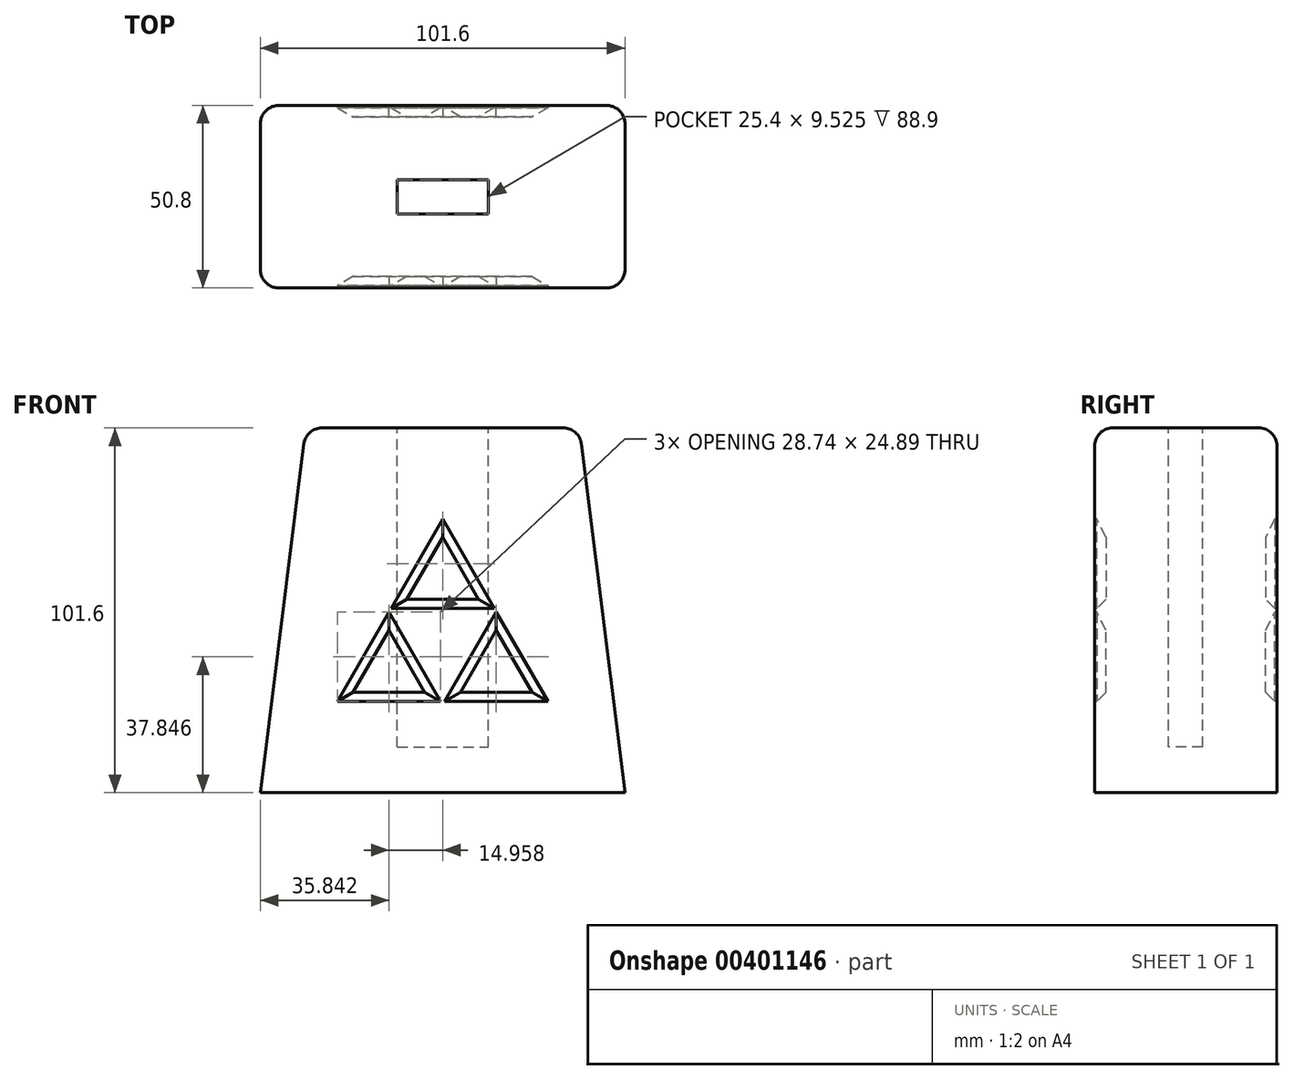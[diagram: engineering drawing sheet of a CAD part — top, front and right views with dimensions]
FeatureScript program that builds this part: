
annotation { "Feature Type Name" : "Feature", "Feature Type Description" : "" }
export const myFeature = defineFeature(function(context is Context, id is Id, definition is map)
    precondition{}
    {
        {
            var Q0;
            Q0=qCreatedBy(makeId("Top.planeOp"),FACE);
            var sketch = newSketch(context, id + "F0", { "sketchPlane" : qUnion([Q0])});
            skLineSegment(sketch, "E0.bottom", {"start": v(-50.8, 25.4) * mm, "end": v(50.8, 25.4) * mm});
            skLineSegment(sketch, "E0.top", {"start": v(-50.8, -25.4) * mm, "end": v(50.8, -25.4) * mm});
            skLineSegment(sketch, "E0.left", {"start": v(-50.8, 25.4) * mm, "end": v(-50.8, -25.4) * mm});
            skLineSegment(sketch, "E0.right", {"start": v(50.8, 25.4) * mm, "end": v(50.8, -25.4) * mm});
            skPoint(sketch, "E0.middle", {"position": v(0, 0) * mm});
            skSolve(sketch);
        }
        {
            var Q0;
            Q0 = qSketchRegion(id + "F0", true);
            extrude(context, id + "F1", {"entities" : qUnion([Q0]), "depth" : 101.6 * mm});
        }
        {
            var Q0;
            Q0=makeQuery(id+"F1.opExtrude","CAP_EDGE",EDGE,{"disambiguationData":[OSD([sQuery(id+"F0.wireOp",EDGE,"E0.right")])],"isStart":false});
            var Q1;
            Q1=makeQuery(id+"F1.opExtrude","CAP_EDGE",EDGE,{"disambiguationData":[OSD([sQuery(id+"F0.wireOp",EDGE,"E0.left")])],"isStart":false});
            chamfer(context, id + "F2", {"entities" : qUnion([Q0, Q1]), "chamferType" : ChamferType.TWO_OFFSETS, "width1" : 101.6 * mm, "oppositeDirection" : false, "width2" : 12.7 * mm, "tangentPropagation" : true});
        }
        {
            var Q0;
            Q0=makeQuery(id+"F1.opExtrude","SWEPT_FACE",FACE,{"disambiguationData":[OSD([sQuery(id+"F0.wireOp",EDGE,"E0.top")])]});
            var sketch = newSketch(context, id + "F3", { "sketchPlane" : qUnion([Q0])});
            skLineSegment(sketch, "E1", {"start": v(0, 76.2) * mm, "end": v(-29.33, 25.4) * mm});
            skPoint(sketch, "E1.startSnap0", {"position": v(0, 101.6) * mm});
            skLineSegment(sketch, "E2", {"start": v(-29.33, 25.4) * mm, "end": v(0, 25.4) * mm});
            skLineSegment(sketch, "E3", {"start": v(0, 25.4) * mm, "end": v(0, 76.2) * mm});
            skLineSegment(sketch, "E4.MirrorCS", {"start": v(0, 76.2) * mm, "end": v(29.33, 25.4) * mm});
            skLineSegment(sketch, "E5.MirrorCS", {"start": v(29.33, 25.4) * mm, "end": v(0, 25.4) * mm});
            skSolve(sketch);
        }
        {
            var Q0;
            Q0=makeQuery(id+"F3.imprint","IMPRINT",FACE,{"disambiguationData":[TD([[makeQuery(id+"F3.imprint","IMPRINT",EDGE,{"derivedFrom":sQuery(id+"F3.wireOp",EDGE,"E1")}),1.0]])]});
            var Q1;
            Q1=makeQuery(id+"F3.imprint","IMPRINT",FACE,{"disambiguationData":[TD([[makeQuery(id+"F3.imprint","IMPRINT",EDGE,{"derivedFrom":sQuery(id+"F3.wireOp",EDGE,"E3")}),-1.0]])]});
            extrude(context, id + "F4", {"entities" : qUnion([Q0, Q1]), "operationType" : NewBodyOperationType.REMOVE, "oppositeDirection" : true, "depth" : 3.17 * mm});
        }
        {
            var Q0;
            Q0 = qSketchRegion(id + "F3", true);
            extrude(context, id + "F5", {"entities" : qUnion([Q0]), "operationType" : NewBodyOperationType.REMOVE, "oppositeDirection" : true, "depth" : 103.89 * mm, "hasSecondDirection" : true, "secondDirectionOppositeDirection" : true, "secondDirectionDepth" : 47.62 * mm});
        }
        {
            var Q0;
            Q0=makeQuery(id+"F5.boolean.opBoolean","COPY",FACE,{"derivedFrom":makeQuery(id+"F5.opExtrude","CAP_FACE",FACE,{"disambiguationData":[OSD([sQuery(id+"F3.wireOp",EDGE,"E1"),sQuery(id+"F3.wireOp",EDGE,"E2"),sQuery(id+"F3.wireOp",EDGE,"E4.MirrorCS"),sQuery(id+"F3.wireOp",EDGE,"E5.MirrorCS")])],"isStart":true})});
            var sketch = newSketch(context, id + "F6", { "sketchPlane" : qUnion([Q0])});
            skLineSegment(sketch, "E6", {"start": v(-14.66, 50.8) * mm, "end": v(-15.54, 51.3) * mm});
            skLineSegment(sketch, "E7", {"start": v(14.66, 50.8) * mm, "end": v(15.54, 51.3) * mm});
            skLineSegment(sketch, "E8", {"start": v(0, 25.4) * mm, "end": v(0, 24.38) * mm});
            skPoint(sketch, "E8.endSnap0", {"position": v(0, 25.4) * mm});
            skLineSegment(sketch, "E9", {"start": v(-15.54, 51.3) * mm, "end": v(15.54, 51.3) * mm});
            skLineSegment(sketch, "E10", {"start": v(0, 24.38) * mm, "end": v(-15.54, 51.3) * mm});
            skLineSegment(sketch, "E11", {"start": v(15.54, 51.3) * mm, "end": v(0, 24.38) * mm});
            skSolve(sketch);
        }
        {
            var Q0;
            Q0 = qSketchRegion(id + "F6", true);
            var Q1;
            Q1=makeQuery(id+"F1.opExtrude","SWEPT_FACE",FACE,{"disambiguationData":[OSD([sQuery(id+"F0.wireOp",EDGE,"E0.bottom")])]});
            var Q2;
            Q2=makeQuery(id+"F1.opExtrude","SWEPT_FACE",FACE,{"disambiguationData":[OSD([sQuery(id+"F0.wireOp",EDGE,"E0.top")])]});
            extrude(context, id + "F7", {"entities" : qUnion([Q0]), "operationType" : NewBodyOperationType.ADD, "endBound" : BoundingType.UP_TO_SURFACE, "endBoundEntityFace" : qUnion([Q1]), "depth" : 25.4 * mm, "hasSecondDirection" : true, "secondDirectionBound" : SecondDirectionBoundingType.UP_TO_SURFACE, "secondDirectionOppositeDirection" : true, "secondDirectionBoundEntityFace" : qUnion([Q2]), "secondDirectionDepth" : 25.4 * mm});
        }
        {
            var Q0;
            Q0=makeQuery(id+"F1.opExtrude","CAP_FACE",FACE,{"disambiguationData":[OSD([sQuery(id+"F0.wireOp",EDGE,"E0.bottom"),sQuery(id+"F0.wireOp",EDGE,"E0.top"),sQuery(id+"F0.wireOp",EDGE,"E0.left"),sQuery(id+"F0.wireOp",EDGE,"E0.right")])],"isStart":false});
            var sketch = newSketch(context, id + "F8", { "sketchPlane" : qUnion([Q0])});
            skLineSegment(sketch, "E12.bottom", {"start": v(-12.7, 4.76) * mm, "end": v(12.7, 4.76) * mm});
            skLineSegment(sketch, "E12.top", {"start": v(-12.7, -4.76) * mm, "end": v(12.7, -4.76) * mm});
            skLineSegment(sketch, "E12.left", {"start": v(-12.7, 4.76) * mm, "end": v(-12.7, -4.76) * mm});
            skLineSegment(sketch, "E12.right", {"start": v(12.7, 4.76) * mm, "end": v(12.7, -4.76) * mm});
            skPoint(sketch, "E12.middle", {"position": v(0, 0) * mm});
            skSolve(sketch);
        }
        {
            var Q0;
            Q0 = qSketchRegion(id + "F8", true);
            extrude(context, id + "F9", {"entities" : qUnion([Q0]), "operationType" : NewBodyOperationType.REMOVE, "oppositeDirection" : true, "depth" : 88.9 * mm});
        }
        {
            var Q0;
            {var subQ0=sQuery(id+"F0.wireOp",EDGE,"E0.left");Q0=makeQuery(id+"F2.opChamfer","BLEND_EDGE",EDGE,{"blendedFrom":[makeQuery(id+"F1.opExtrude","CAP_EDGE",EDGE,{"disambiguationData":[OSD([subQ0])],"isStart":false}),makeQuery(id+"F1.opExtrude","CAP_FACE",FACE,{"disambiguationData":[OSD([sQuery(id+"F0.wireOp",EDGE,"E0.bottom"),sQuery(id+"F0.wireOp",EDGE,"E0.top"),subQ0,sQuery(id+"F0.wireOp",EDGE,"E0.right")])],"isStart":false})],"blendedInto":[makeQuery(id+"F1.opExtrude","CAP_FACE",FACE,{"disambiguationData":[OSD([sQuery(id+"F0.wireOp",EDGE,"E0.bottom"),sQuery(id+"F0.wireOp",EDGE,"E0.top"),subQ0,sQuery(id+"F0.wireOp",EDGE,"E0.right")])],"isStart":false})]});}
            var Q1;
            Q1=makeQuery(id+"F1.opExtrude","CAP_EDGE",EDGE,{"disambiguationData":[OSD([sQuery(id+"F0.wireOp",EDGE,"E0.bottom")])],"isStart":false});
            var Q2;
            {var subQ0=sQuery(id+"F0.wireOp",EDGE,"E0.right");Q2=makeQuery(id+"F2.opChamfer","BLEND_EDGE",EDGE,{"blendedFrom":[makeQuery(id+"F1.opExtrude","CAP_EDGE",EDGE,{"disambiguationData":[OSD([subQ0])],"isStart":false}),makeQuery(id+"F1.opExtrude","CAP_FACE",FACE,{"disambiguationData":[OSD([sQuery(id+"F0.wireOp",EDGE,"E0.bottom"),sQuery(id+"F0.wireOp",EDGE,"E0.top"),sQuery(id+"F0.wireOp",EDGE,"E0.left"),subQ0])],"isStart":false})],"blendedInto":[makeQuery(id+"F1.opExtrude","CAP_FACE",FACE,{"disambiguationData":[OSD([sQuery(id+"F0.wireOp",EDGE,"E0.bottom"),sQuery(id+"F0.wireOp",EDGE,"E0.top"),sQuery(id+"F0.wireOp",EDGE,"E0.left"),subQ0])],"isStart":false})]});}
            var Q3;
            Q3=makeQuery(id+"F1.opExtrude","CAP_EDGE",EDGE,{"disambiguationData":[OSD([sQuery(id+"F0.wireOp",EDGE,"E0.top")])],"isStart":false});
            var Q4;
            Q4=makeQuery(id+"F2.opChamfer","BLEND_EDGE",EDGE,{"blendedFrom":[makeQuery(id+"F1.opExtrude","CAP_EDGE",EDGE,{"disambiguationData":[OSD([sQuery(id+"F0.wireOp",EDGE,"E0.left")])],"isStart":false}),makeQuery(id+"F1.opExtrude","SWEPT_FACE",FACE,{"disambiguationData":[OSD([sQuery(id+"F0.wireOp",EDGE,"E0.bottom")])]})],"blendedInto":[makeQuery(id+"F1.opExtrude","SWEPT_FACE",FACE,{"disambiguationData":[OSD([sQuery(id+"F0.wireOp",EDGE,"E0.bottom")])]})]});
            var Q5;
            Q5=makeQuery(id+"F2.opChamfer","BLEND_EDGE",EDGE,{"blendedFrom":[makeQuery(id+"F1.opExtrude","CAP_EDGE",EDGE,{"disambiguationData":[OSD([sQuery(id+"F0.wireOp",EDGE,"E0.left")])],"isStart":false}),makeQuery(id+"F1.opExtrude","SWEPT_FACE",FACE,{"disambiguationData":[OSD([sQuery(id+"F0.wireOp",EDGE,"E0.top")])]})],"blendedInto":[makeQuery(id+"F1.opExtrude","SWEPT_FACE",FACE,{"disambiguationData":[OSD([sQuery(id+"F0.wireOp",EDGE,"E0.top")])]})]});
            var Q6;
            Q6=makeQuery(id+"F2.opChamfer","BLEND_EDGE",EDGE,{"blendedFrom":[makeQuery(id+"F1.opExtrude","CAP_EDGE",EDGE,{"disambiguationData":[OSD([sQuery(id+"F0.wireOp",EDGE,"E0.right")])],"isStart":false}),makeQuery(id+"F1.opExtrude","SWEPT_FACE",FACE,{"disambiguationData":[OSD([sQuery(id+"F0.wireOp",EDGE,"E0.bottom")])]})],"blendedInto":[makeQuery(id+"F1.opExtrude","SWEPT_FACE",FACE,{"disambiguationData":[OSD([sQuery(id+"F0.wireOp",EDGE,"E0.bottom")])]})]});
            var Q7;
            Q7=makeQuery(id+"F2.opChamfer","BLEND_EDGE",EDGE,{"blendedFrom":[makeQuery(id+"F1.opExtrude","CAP_EDGE",EDGE,{"disambiguationData":[OSD([sQuery(id+"F0.wireOp",EDGE,"E0.right")])],"isStart":false}),makeQuery(id+"F1.opExtrude","SWEPT_FACE",FACE,{"disambiguationData":[OSD([sQuery(id+"F0.wireOp",EDGE,"E0.top")])]})],"blendedInto":[makeQuery(id+"F1.opExtrude","SWEPT_FACE",FACE,{"disambiguationData":[OSD([sQuery(id+"F0.wireOp",EDGE,"E0.top")])]})]});
            fillet(context, id + "F10", {"entities" : qUnion([Q0, Q1, Q2, Q3, Q4, Q5, Q6, Q7]), "radius" : 5.08 * mm, "tangentPropagation" : true, "allowEdgeOverflow" : false});
        }
        {
            var Q0;
            {var subQ0=sQuery(id+"F3.wireOp",EDGE,"E1");var subQ1=sQuery(id+"F3.wireOp",EDGE,"E4.MirrorCS");Q0=makeQuery(id+"F7.boolean.opBoolean","SPLIT",FACE,{"disambiguationData":[TD([makeQuery(id+"F7.opExtrude","SWEPT_FACE",FACE,{"disambiguationData":[OSD([sQuery(id+"F6.wireOp",EDGE,"E9")])]})])],"derivedFrom":makeQuery(id+"F4.boolean.opBoolean","COPY",FACE,{"derivedFrom":makeQuery(id+"F4.opExtrude","CAP_FACE",FACE,{"disambiguationData":[OSD([subQ0,sQuery(id+"F3.wireOp",EDGE,"E2"),subQ1,sQuery(id+"F3.wireOp",EDGE,"E5.MirrorCS")])],"isStart":false})})});}
            var Q1;
            {var subQ0=sQuery(id+"F3.wireOp",EDGE,"E5.MirrorCS");var subQ1=sQuery(id+"F3.wireOp",EDGE,"E2");var subQ2=sQuery(id+"F3.wireOp",EDGE,"E4.MirrorCS");Q1=makeQuery(id+"F7.boolean.opBoolean","SPLIT",FACE,{"disambiguationData":[TD([makeQuery(id+"F7.opExtrude","SWEPT_FACE",FACE,{"disambiguationData":[OSD([sQuery(id+"F6.wireOp",EDGE,"E10")])]})])],"derivedFrom":makeQuery(id+"F4.boolean.opBoolean","COPY",FACE,{"derivedFrom":makeQuery(id+"F4.opExtrude","CAP_FACE",FACE,{"disambiguationData":[OSD([sQuery(id+"F3.wireOp",EDGE,"E1"),subQ1,subQ2,subQ0])],"isStart":false})})});}
            var Q2;
            {var subQ0=sQuery(id+"F3.wireOp",EDGE,"E1");var subQ1=sQuery(id+"F3.wireOp",EDGE,"E5.MirrorCS");var subQ2=sQuery(id+"F3.wireOp",EDGE,"E2");Q2=makeQuery(id+"F7.boolean.opBoolean","SPLIT",FACE,{"disambiguationData":[TD([makeQuery(id+"F7.opExtrude","SWEPT_FACE",FACE,{"disambiguationData":[OSD([sQuery(id+"F6.wireOp",EDGE,"E11")])]})])],"derivedFrom":makeQuery(id+"F4.boolean.opBoolean","COPY",FACE,{"derivedFrom":makeQuery(id+"F4.opExtrude","CAP_FACE",FACE,{"disambiguationData":[OSD([subQ0,subQ2,sQuery(id+"F3.wireOp",EDGE,"E4.MirrorCS"),subQ1])],"isStart":false})})});}
            var Q3;
            {var subQ0=sQuery(id+"F3.wireOp",EDGE,"E1");var subQ1=sQuery(id+"F3.wireOp",EDGE,"E4.MirrorCS");Q3=makeQuery(id+"F7.boolean.opBoolean","SPLIT",FACE,{"disambiguationData":[TD([makeQuery(id+"F7.opExtrude","SWEPT_FACE",FACE,{"disambiguationData":[OSD([sQuery(id+"F6.wireOp",EDGE,"E9")])]})])],"derivedFrom":makeQuery(id+"F5.boolean.opBoolean","COPY",FACE,{"derivedFrom":makeQuery(id+"F5.opExtrude","CAP_FACE",FACE,{"disambiguationData":[OSD([subQ0,sQuery(id+"F3.wireOp",EDGE,"E2"),subQ1,sQuery(id+"F3.wireOp",EDGE,"E5.MirrorCS")])],"isStart":true})})});}
            var Q4;
            {var subQ0=sQuery(id+"F3.wireOp",EDGE,"E5.MirrorCS");var subQ1=sQuery(id+"F3.wireOp",EDGE,"E2");var subQ2=sQuery(id+"F3.wireOp",EDGE,"E4.MirrorCS");Q4=makeQuery(id+"F7.boolean.opBoolean","SPLIT",FACE,{"disambiguationData":[TD([makeQuery(id+"F7.opExtrude","SWEPT_FACE",FACE,{"disambiguationData":[OSD([sQuery(id+"F6.wireOp",EDGE,"E10")])]})])],"derivedFrom":makeQuery(id+"F5.boolean.opBoolean","COPY",FACE,{"derivedFrom":makeQuery(id+"F5.opExtrude","CAP_FACE",FACE,{"disambiguationData":[OSD([sQuery(id+"F3.wireOp",EDGE,"E1"),subQ1,subQ2,subQ0])],"isStart":true})})});}
            var Q5;
            {var subQ0=sQuery(id+"F3.wireOp",EDGE,"E1");var subQ1=sQuery(id+"F3.wireOp",EDGE,"E5.MirrorCS");var subQ2=sQuery(id+"F3.wireOp",EDGE,"E2");Q5=makeQuery(id+"F7.boolean.opBoolean","SPLIT",FACE,{"disambiguationData":[TD([makeQuery(id+"F7.opExtrude","SWEPT_FACE",FACE,{"disambiguationData":[OSD([sQuery(id+"F6.wireOp",EDGE,"E11")])]})])],"derivedFrom":makeQuery(id+"F5.boolean.opBoolean","COPY",FACE,{"derivedFrom":makeQuery(id+"F5.opExtrude","CAP_FACE",FACE,{"disambiguationData":[OSD([subQ0,subQ2,sQuery(id+"F3.wireOp",EDGE,"E4.MirrorCS"),subQ1])],"isStart":true})})});}
            chamfer(context, id + "F11", {"entities" : qUnion([Q0, Q1, Q2, Q3, Q4, Q5]), "width" : 2.54 * mm, "tangentPropagation" : true});
        }
    });
